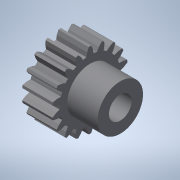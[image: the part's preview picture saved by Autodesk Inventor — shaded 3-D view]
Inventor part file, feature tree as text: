
AUTODESK INVENTOR PART (.ipt)
format: ipt  version: 2020.2 (Build 242310000, 310)  size: 231,936 bytes
history: native  units: mm
features: hole x1, imported_body x1, sketch x1
ambient origin geometry x8: Origin, YZ Plane, XZ Plane, XY Plane, X Axis, Y Axis, Z Axis, Center Point
bodies: Body1 (feature_tree)
feature tree (3):
  hole  "Bohrung1"  [1 undecoded]
  imported_body  "Basis1"
  sketch  "Skizze1"  dims[d0=4.0mm d1=6.0mm d2=4.0mm d3=2.0mm d4=90.0deg d5=8.0mm d6=20.594885mm]
note: 1 required parameter value undecoded (feature->parameter linkage not recoverable at this tier; creation-order binding heuristic only, values carry confidence <= 0.55)
